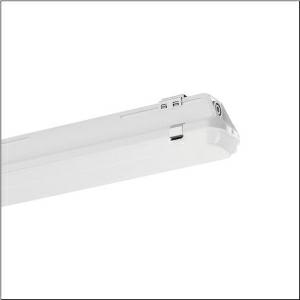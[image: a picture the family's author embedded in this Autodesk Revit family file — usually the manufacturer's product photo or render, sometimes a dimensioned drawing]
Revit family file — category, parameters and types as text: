
# Revit family: monsun_r__11_parking_51fg20dp440hhq_4cc6
name_source: partatom
category: Lighting Fixtures
units: mm (PartAtom-declared; Revit-internal decimal feet)

## family parameters
Cut with Voids When Loaded = No
Host = Face
Light Source = No
Part Type = Normal
Room Calculation Point = No
Round Connector Dimension = Use Diameter
Shared = No

## types (1)
- --- (1 x LED, 4840 lm, 31.3 W, 4000K)
    Apparent Load = 31 VA
    CIE Flux Codes = 45 75 93 94 100
    Color Rendering = 80
    Color Temperature = 4000K
    Default Elevation = 1800 mm
    Description = Monsun® 11 parking, damp-proof luminaire, chain hanger, primary optical cover: enclosure, of PC, light emission: direct distribution, primary light characteristic: symmetric, installation type: suspended mounting, surface-mounted, horizontal mounting, vertical mounting, LED, rated luminous flux: 4.840lm, luminous efficacy: 157lm/W, light colour: 840, colour temperature: 4000K, control gear: ECG DALI, with terminal, 5-pole, max. 2.5mm², mains connection: 220..240V, AC, 50/60Hz, rated input power: 31W, housing, of glass-fibre reinforced polyester, uncoated, bright grey, length: 1.590mm, width: 90mm, height: 88mm, clip for enclosure, of stainless steel (V2A), ceiling mounting element, of stainless steel (V2A), chain hanger, of stainless steel (V2A), multi-sensor HC1, local controlcentral control, equipment: slave, scope of services: certified according to part 101,103,303,304, protection rating (complete): IP66, insulation class (complete): insulation class I (protective earthing), certification: CE, ENEC, VDE, UKCA, protection symbol: D, impact resistance: IK08, permissible operating ambient temperature: -25..+40°C, standard: EN 50419, EN 60598-2-1, corresponds to IFS (International Featured Standards) requirements for safety and quality in the food industry, for indoor or canopied outdoor use, no direct snow, no direct sun, no direct rain, packaging unit: 1 piece
    Height = 89 mm
    Lamp = 1 x LED
    Lamp Light Flux = 4840 lm
    Lamp Power = 31.3 W
    Lamp count = 1
    Length = 1590 mm
    Luminous efficacy = 155 lm/W
    Manufacturer = Siteco
    ModVariant = No
    Model = 51FG20DP440HHQ
    Mounting Place = Ceiling
    Mounting Type = Pendant
    Number of Poles = 1
    OnlyDefault = Yes
    Power Factor = 1
    Product Name = Monsun® 11 parking
    Product group = damp-proof luminaire | ceiling pendant
    ProductGroupID = 908
    Protection Class = Protection class I
    Protection Degree = IP 66
    RLX_Detail_Level = 1
    RlxData = <blob elided: 92257 chars, md5=a7abccd1>
    Socket = socket
    Standby Power = 0 W
    System Light Flux = 4840 lm
    System Power = 31 W
    Type Comments = factory setting: luminous flux: 100 % | dim-lin: 254 | 205 mA
    Type Image = l_1004748.jpg
    URL = http://relux.com
    VarID = @adj_049603
    Voltage = 0 V
    Weight = 0.00 kg
    Width = 90 mm

## geometry (parser evidence)
native form markers: Blend x4, Sweep x12
no freeform markers — native parametric forms only
